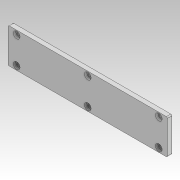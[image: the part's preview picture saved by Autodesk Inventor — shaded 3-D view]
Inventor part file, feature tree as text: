
AUTODESK INVENTOR PART (.ipt)
format: ipt  version: 2020 (Build 240168000, 168)  size: 122,368 bytes
history: native  units: mm
features: extrude x2, sketch x2
ambient origin geometry x8: Origin, YZ Plane, XZ Plane, XY Plane, X Axis, Y Axis, Z Axis, Center Point
bodies: Solid1 (feature_tree)
feature tree (4):
  extrude  "Extrusion1"  Depth=31.5mm
  extrude  "Extrusion2"  Depth=12.0mm
  sketch  "Sketch1"  dims[d0=144.0mm d1=31.5mm]
  sketch  "Sketch2"  dims[d2=64.25mm d3=12.0mm d4=3.5mm d5=1.0mm d6=4.0mm d7=0.0mm d8=6.0mm d9=2.2mm d10=0.0mm]
